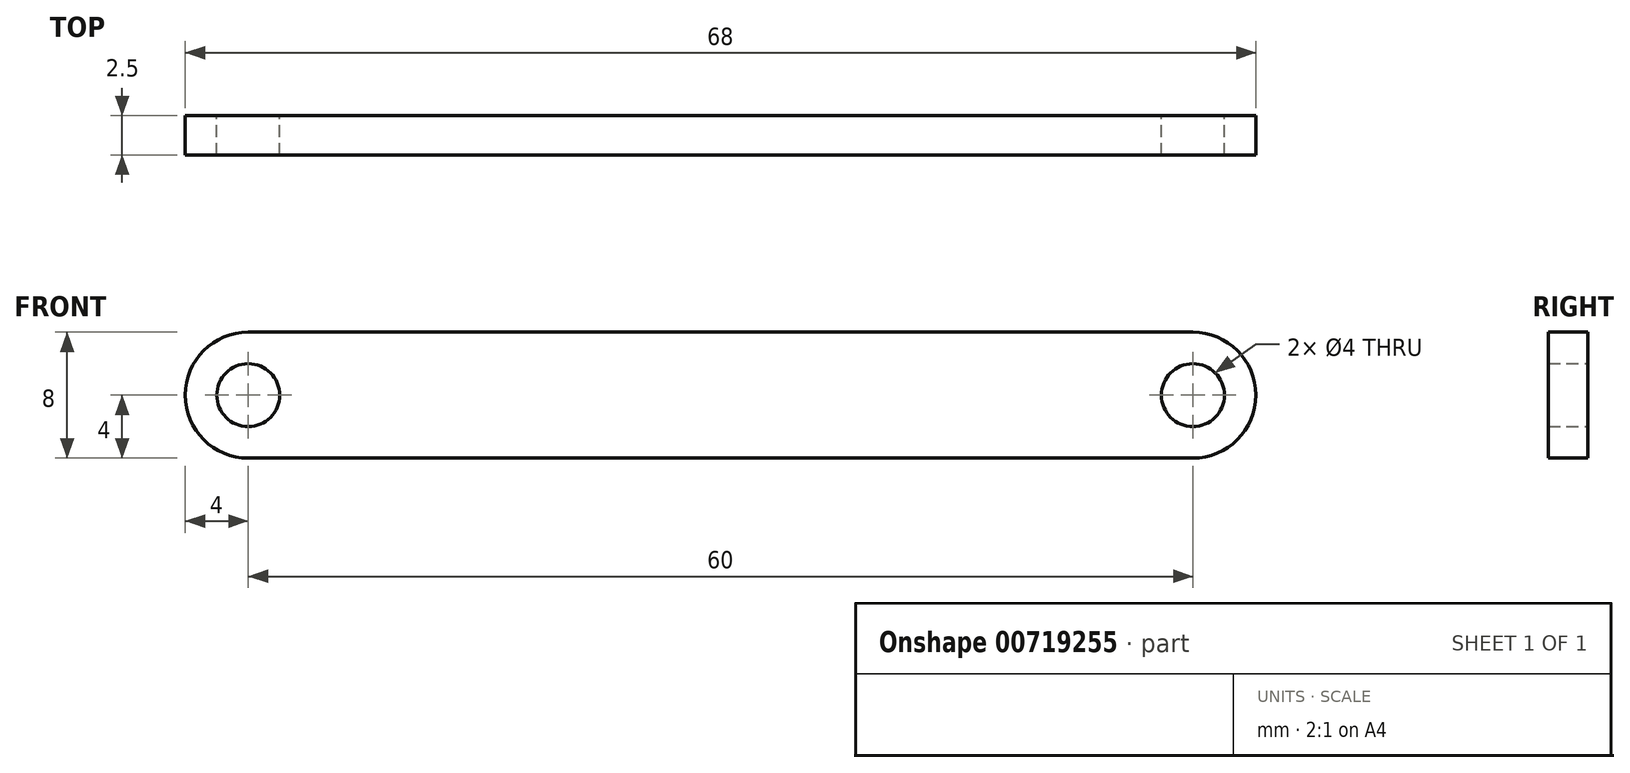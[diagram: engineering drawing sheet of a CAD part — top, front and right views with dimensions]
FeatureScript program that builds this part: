
annotation { "Feature Type Name" : "Feature", "Feature Type Description" : "" }
export const myFeature = defineFeature(function(context is Context, id is Id, definition is map)
    precondition{}
    {
        {
            var Q0;
            Q0=qCreatedBy(makeId("Front.planeOp"),FACE);
            var sketch = newSketch(context, id + "F0", { "sketchPlane" : qUnion([Q0])});
            skArc(sketch, "E0", {"start": v(0, -4) * mm, "mid": v(4, 0) * mm, "end": v(0, 4) * mm});
            skArc(sketch, "E1", {"start": v(-60, 4) * mm, "mid": v(-64, 0) * mm, "end": v(-60, -4) * mm});
            skLineSegment(sketch, "E2", {"start": v(0, 4) * mm, "end": v(-60, 4) * mm});
            skLineSegment(sketch, "E3", {"start": v(0, -4) * mm, "end": v(-60, -4) * mm});
            skCircle(sketch, "E4", {"center": v(-60, 0) * mm, "radius": 2 * mm});
            skCircle(sketch, "E5", {"center": v(0, 0) * mm, "radius": 2 * mm});
            skSolve(sketch);
        }
        {
            var Q0;
            Q0 = qSketchRegion(id + "F0", true);
            extrude(context, id + "F1", {"entities" : qUnion([Q0]), "depth" : 2.5 * mm, "offsetDistance" : 25.4 * mm});
        }
    });
